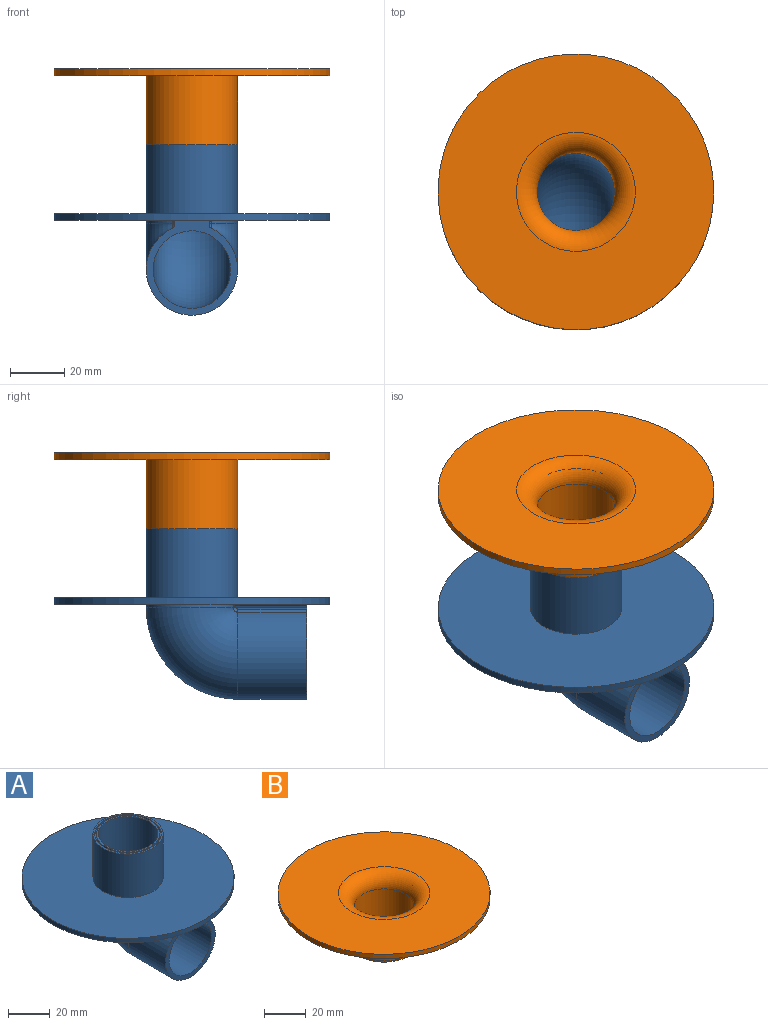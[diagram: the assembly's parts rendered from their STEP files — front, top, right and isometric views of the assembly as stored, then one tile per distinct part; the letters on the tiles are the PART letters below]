
ASSEMBLY  parts=2 mates=1
PART A: 26 faces, bbox 101.6x101.6x65.6 mm
  f0: plane 101.6x101.6mm, normal (0,0,-1), area 6821.6mm2, adj f1,f7,f15,f19,f23
  f1: cylinder r=16.83mm len=33.66mm, axis (0,0,1), area 115.7mm2, adj f0,f2,f19,f21,f23,f25
  f2: torus R=16.83mm, axis (1,0,0), area 2782.7mm2, adj f1,f3,f20,f24
  f3: cylinder r=16.83mm len=33.66mm, axis (0,1,0), area 2314mm2, adj f2,f15,f18,f22
  f4: plane 30.35x30.35mm, normal (0,0,1), area 82.3mm2, adj f5,f12
  f5: cylinder r=14.29mm len=29.21mm, axis (0,0,-1), area 2622.2mm2, adj f4,f9
  f6: cylinder r=16.83mm len=33.66mm, axis (0,0,-1), area 2685.5mm2, adj f8,f10
  f7: cylinder r=50.8mm len=101.6mm, axis (0,0,-1), area 810.7mm2, adj f0,f8
  f8: plane 101.6x101.6mm, normal (0,0,1), area 7217.7mm2, adj f6,f7
  f9: torus R=16.83mm, axis (1,0,0), area 2372.9mm2, adj f5,f14
  f10: plane 33.66x33.66mm, normal (0,0,1), area 91.5mm2, adj f6,f11
  f11: cylinder r=15.94mm len=31.88mm, axis (0,0,1), area 127.2mm2, adj f10,f13
  f12: cylinder r=15.18mm len=30.35mm, axis (0,0,1), area 121.1mm2, adj f4,f13
  f13: plane 31.88x31.88mm, normal (0,0,1), area 74.5mm2, adj f11,f12
  f14: cylinder r=14.29mm len=28.58mm, axis (0,1,0), area 2280.2mm2, adj f9,f15
  f15: plane 34.93x33.66mm, normal (0,-1,0), area 270.5mm2, adj f0,f3,f14,f16,f17,f18,f19,f22
  f16: plane 25.81x0.41mm, normal (-1,0,0), area 10.6mm2, adj f15,f22,f23,f24
  f17: plane 25.81x0.41mm, normal (1,0,0), area 10.6mm2, adj f15,f18,f19,f20
  f18: cylinder r=1.27mm len=25.4mm, axis (0,1,0), area 36.7mm2, adj f3,f15,f17,f20
  f19: cylinder r=1.27mm len=27.22mm, axis (0,-1,0), area 53.1mm2, adj f0,f1,f15,f17,f21
  f20: torus R=0.41mm, axis (-1,0,0), area 2.4mm2, adj f2,f17,f18,f21
  f21: cylinder r=1.27mm len=1.15mm, axis (0,0,1), area 0.9mm2, adj f1,f19,f20
  f22: cylinder r=1.27mm len=25.4mm, axis (0,1,0), area 36.7mm2, adj f3,f15,f16,f24
  f23: cylinder r=1.27mm len=27.22mm, axis (0,1,0), area 53.1mm2, adj f0,f1,f15,f16,f25
  f24: torus R=0.41mm, axis (-1,0,0), area 2.4mm2, adj f2,f16,f22,f25
  f25: cylinder r=1.27mm len=1.15mm, axis (0,0,1), area 0.9mm2, adj f1,f23,f24
PART B: 11 faces, bbox 101.6x101.6x29.2 mm
  f0: plane 30.35x30.35mm, normal (0,0,-1), area 82.3mm2, adj f2,f8
  f1: plane 101.6x101.6mm, normal (0,0,1), area 6599.5mm2, adj f3,f10
  f2: cylinder r=14.29mm len=28.58mm, axis (0,0,-1), area 1824.1mm2, adj f0,f10
  f3: cylinder r=50.8mm len=101.6mm, axis (0,0,-1), area 810.7mm2, adj f1,f4
  f4: plane 101.6x101.6mm, normal (0,0,-1), area 7217.7mm2, adj f3,f5
  f5: cylinder r=16.83mm len=33.66mm, axis (0,0,-1), area 2685.5mm2, adj f4,f6
  f6: plane 33.66x33.66mm, normal (0,0,-1), area 91.5mm2, adj f5,f7
  f7: cylinder r=15.94mm len=31.88mm, axis (0,0,-1), area 127.2mm2, adj f6,f9
  f8: cylinder r=15.18mm len=30.35mm, axis (0,0,-1), area 121.1mm2, adj f0,f9
  f9: plane 31.88x31.88mm, normal (0,0,-1), area 74.5mm2, adj f7,f8
  f10: torus R=21.91mm, axis (0,0,1), area 1282.8mm2, adj f1,f2
PLACE A t=(-4.76,12.41,5.33)mm
PLACE B t=(-4.76,12.41,5.33)mm
MATE fastened A.f1 <-> B.f2  axis (0,0,1) through (-4.76,12.41,32)mm
